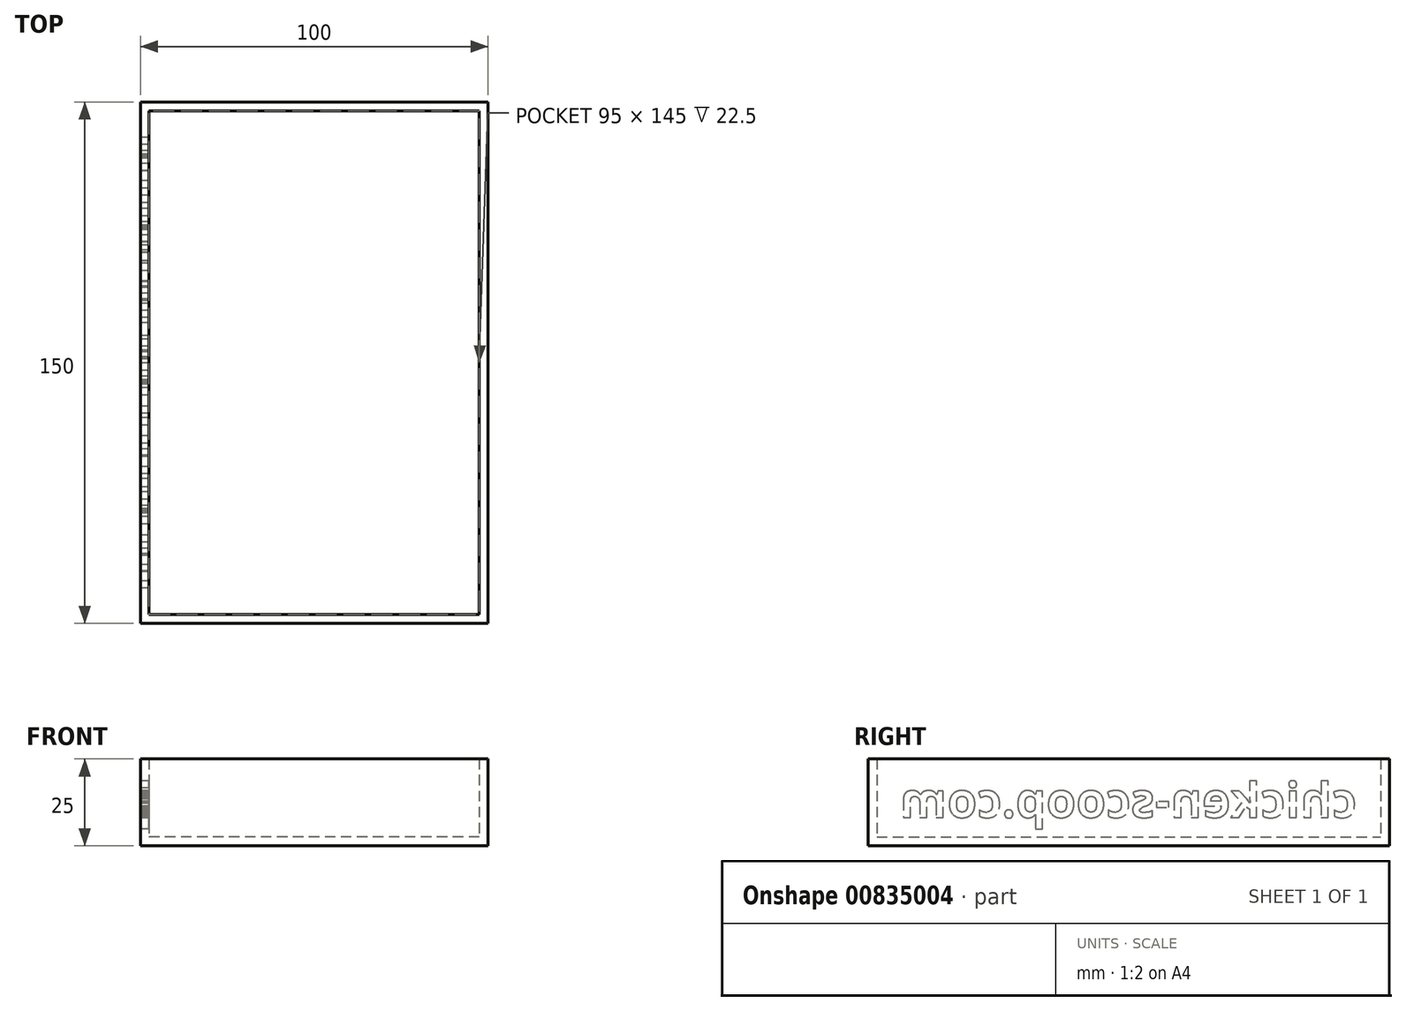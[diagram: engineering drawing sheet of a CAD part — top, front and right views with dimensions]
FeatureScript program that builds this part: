
annotation { "Feature Type Name" : "Feature", "Feature Type Description" : "" }
export const myFeature = defineFeature(function(context is Context, id is Id, definition is map)
    precondition{}
    {
        {
            var Q0;
            Q0=qCreatedBy(makeId("Top.planeOp"),FACE);
            var sketch = newSketch(context, id + "F0", { "sketchPlane" : qUnion([Q0])});
            skLineSegment(sketch, "E0.bottom", {"start": v(50, -75) * mm, "end": v(-50, -75) * mm});
            skLineSegment(sketch, "E0.top", {"start": v(50, 75) * mm, "end": v(-50, 75) * mm});
            skLineSegment(sketch, "E0.left", {"start": v(50, -75) * mm, "end": v(50, 75) * mm});
            skLineSegment(sketch, "E0.right", {"start": v(-50, -75) * mm, "end": v(-50, 75) * mm});
            skPoint(sketch, "E0.middle", {"position": v(0, 0) * mm});
            skLineSegment(sketch, "E1.0", {"start": v(47.5, 72.5) * mm, "end": v(-47.5, 72.5) * mm});
            skLineSegment(sketch, "E1.1", {"start": v(47.5, -72.5) * mm, "end": v(47.5, 72.5) * mm});
            skLineSegment(sketch, "E1.2", {"start": v(47.5, -72.5) * mm, "end": v(-47.5, -72.5) * mm});
            skLineSegment(sketch, "E1.3", {"start": v(-47.5, -72.5) * mm, "end": v(-47.5, 72.5) * mm});
            skSolve(sketch);
        }
        {
            var Q0;
            Q0=makeQuery(id+"F0.imprint","IMPRINT",FACE,{"disambiguationData":[TD([[makeQuery(id+"F0.imprint","IMPRINT",EDGE,{"derivedFrom":sQuery(id+"F0.wireOp",EDGE,"E0.bottom")}),-1.0]])]});
            extrude(context, id + "F1", {"entities" : qUnion([Q0]), "depth" : 25 * mm, "offsetDistance" : 25 * mm});
        }
        {
            var Q0;
            Q0=makeQuery(id+"F0.imprint","IMPRINT",FACE,{"disambiguationData":[TD([[makeQuery(id+"F0.imprint","IMPRINT",EDGE,{"derivedFrom":sQuery(id+"F0.wireOp",EDGE,"E1.0")}),1.0]])]});
            extrude(context, id + "F2", {"entities" : qUnion([Q0]), "operationType" : NewBodyOperationType.ADD, "depth" : 2.5 * mm, "offsetDistance" : 25 * mm});
        }
        {
            var Q0;
            Q0=makeQuery(id+"F1.opExtrude","SWEPT_FACE",FACE,{"disambiguationData":[OSD([sQuery(id+"F0.wireOp",EDGE,"E0.right")])]});
            var sketch = newSketch(context, id + "F3", { "sketchPlane" : qUnion([Q0])});
            skText(sketch, "E2", { "text": "chicken-scoop.com", "fontName": "OpenSans-Bold.ttf"});
            const initialGuessF3  = {"E2": [-0.06552, 0.00817, 1, 0, 0.01]};
            skSetInitialGuess(sketch, initialGuessF3);
            skSolve(sketch);
        }
        {
            var Q0;
            Q0 = qSketchRegion(id + "F3", true);
            extrude(context, id + "F4", {"entities" : qUnion([Q0]), "operationType" : NewBodyOperationType.REMOVE, "oppositeDirection" : true, "depth" : 3 * mm, "offsetDistance" : 25 * mm});
        }
    });
